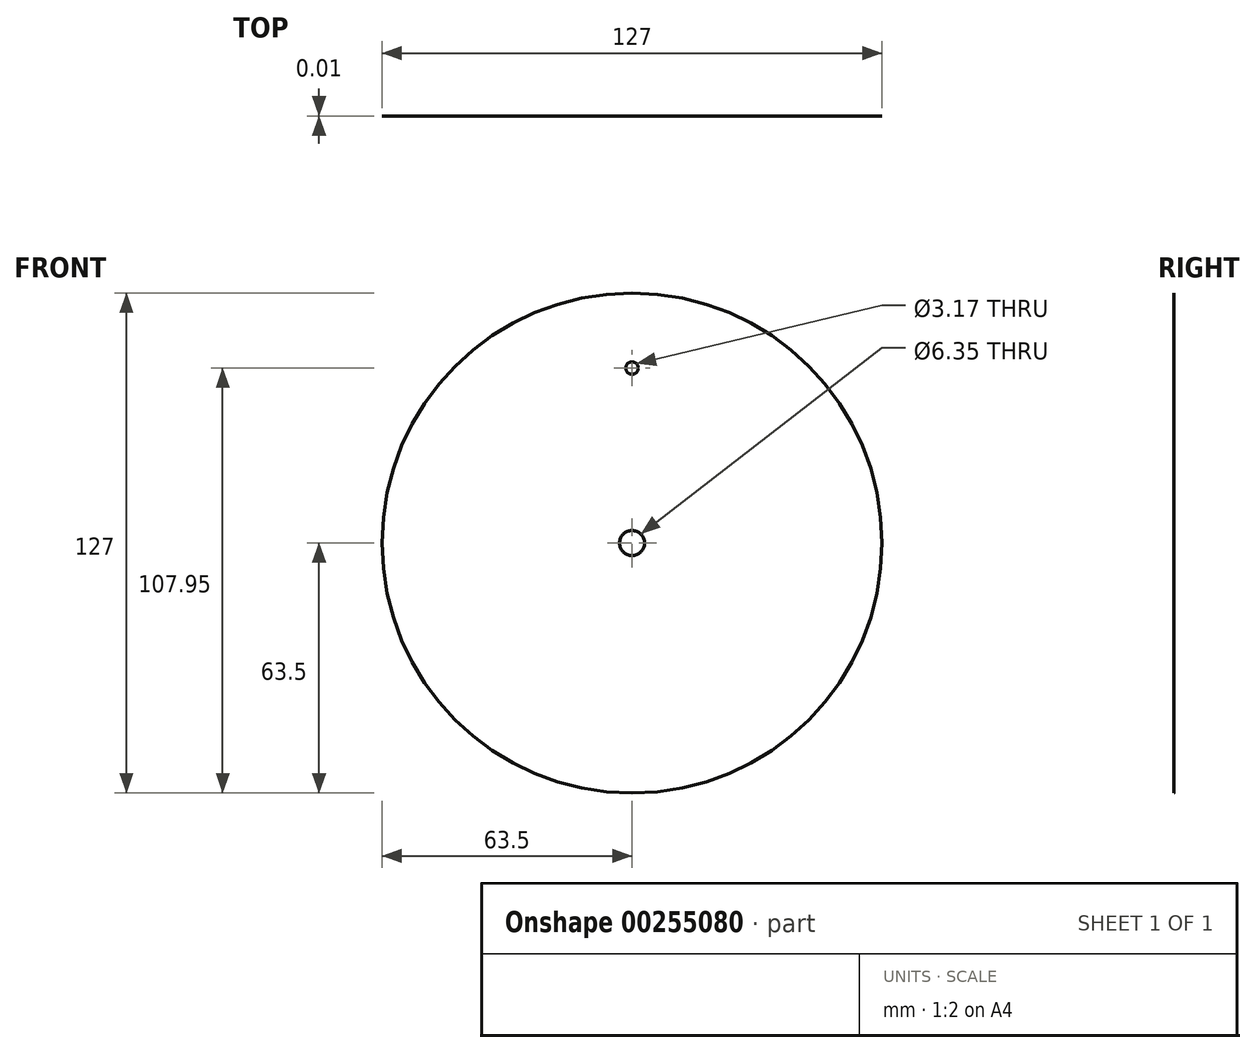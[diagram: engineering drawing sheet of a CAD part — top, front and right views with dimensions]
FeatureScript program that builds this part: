
annotation { "Feature Type Name" : "Feature", "Feature Type Description" : "" }
export const myFeature = defineFeature(function(context is Context, id is Id, definition is map)
    precondition{}
    {
        {
            var Q0;
            Q0=qCreatedBy(makeId("Front.planeOp"),FACE);
            var sketch = newSketch(context, id + "F0", { "sketchPlane" : qUnion([Q0])});
            skCircle(sketch, "E0", {"center": v(0, 0) * mm, "radius": 3.18 * mm});
            skCircle(sketch, "E1", {"center": v(0, 0) * mm, "radius": 63.5 * mm});
            skCircle(sketch, "E2", {"center": v(0, 44.45) * mm, "radius": 1.59 * mm});
            skSolve(sketch);
        }
        {
            var Q0;
            Q0 = qSketchRegion(id + "F0", true);
            extrude(context, id + "F1", {"entities" : qUnion([Q0]), "depth" : 1 / 101.6 * mm});
        }
    });
